# Revit family: QF_COLDLINE_A30-1M
name_source: partatom
category: Specialty Equipment
revit_build: Autodesk Revit 2018 (Build: 20170223_1515(x64)
units: mm (PartAtom-declared; Revit-internal decimal feet)

## family parameters
Always vertical = Yes
Cut with Voids When Loaded = No
Part Type = Normal
Room Calculation Point = No
Round Connector Dimension = Use Diameter
Shared = No
Work Plane-Based = No

## types (1)
- H 2085 mm_A14030200101-Master 350 lt cabinet -2°+8°C 1 door
    24h consumption = 0,89 kW/h/24h
    Absorbed Current = 1,2 A
    Accessory = No
    Annual consumption = 324 kW/h annum
    Apparent Power = 220 VA
    Assembly Code = A14030200101
    Castor Roller = Roller Castor
    Climate Class = 5
    Conn Conduit = No
    Cooling capacity = 406 W*
    Cooling gas = R290
    Cycle = 50 Hz
    Defrost = Hot gas
    Depth Actual = 715 mm  [stored 2.3458 ft]
    Depth of Plinth = 650 mm
    Depth of Table = 715 mm  [stored 2.3458 ft]
    Description = Master 350 lt cabinet -2°+8°C 1 door
    Dimension = 535×715×2085 mm
    Door-2 = Door single_Left : Single
    Door-3 = Door Half_Left : Single
    Door-4 = Door Half_Right : Single
    Electric power = 406 W
    Energetic class = B
    Energy efficiency index = 33,1
    Glaze Frame Width = 80 mm  [stored 0.262467 ft]
    Gross Capacity = 334 lt
    Height Actual = 913 mm
    Length Actual = 535 mm  [stored 1.75525 ft]
    Length of Table = 535 mm  [stored 1.75525 ft]
    Main switch integrated = No
    Manufacturer = Coldline
    Model = A30/1M
    National Water Regulation Certification = No
    No Load Power Draw = No
    Number of Poles = 1
    Odor Trap Included = No
    Operational Current = 1 A
    Packing dimensions = 835×830×2250 mm
    Phase = 1
    Potential Equalisation = No
    Refrigerant Compressor Remote = No
    Refrigeration Defrost Drain = No
    Refrigerent Unit = Plug-In
    Start Up Current = 1 A
    Table Height = 1985 mm
    Table L Top = No
    Table L top = 140 mm
    Table Top = 126 mm  [stored 0.413386 ft]
    Table Top Plain = Yes
    Temp. Range = -2°+8°C
    Total rate = 260 W
    URL Cutsheet = https://coldline.it
    URL Manufacturer = https://coldline.it
    Valve = Supplied standard with solenoid
    Volt Free Conn = No
    Voltage = 220-240 V - 50 Hz
    Volts = 240 V
    Weight = 115.00 kg
    Width Of Door = 470 mm  [stored 1.54199 ft]

note: [stored X ft] marks values corroborated as IEEE doubles in the binary element streams (Revit-internal decimal feet)

## geometry (parser evidence)
native form markers: Sweep x52
no freeform markers — native parametric forms only
